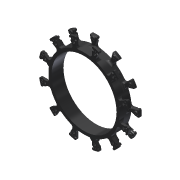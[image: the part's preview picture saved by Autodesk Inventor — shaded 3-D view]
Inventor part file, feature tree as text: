
AUTODESK INVENTOR PART (.ipt)
format: ipt  version: 2013 (Build 170138000, 138)  size: 2,452,992 bytes
history: native  units: in
note: dims shown in document units (in); Inventor stores cm internally (conversion verified against a paired STEP export)
features: fillet x1, other x1, imported_body x1
ambient origin geometry x8: Origin, YZ Plane, XZ Plane, XY Plane, X Axis, Y Axis, Z Axis, Center Point
feature tree (3):
  fillet  "Fillet17"  [1 undecoded]
  other  "217-2585-002 Rev11"
  imported_body  "Base1"
note: 1 required parameter value undecoded (feature->parameter linkage not recoverable at this tier; creation-order binding heuristic only, values carry confidence <= 0.55)
